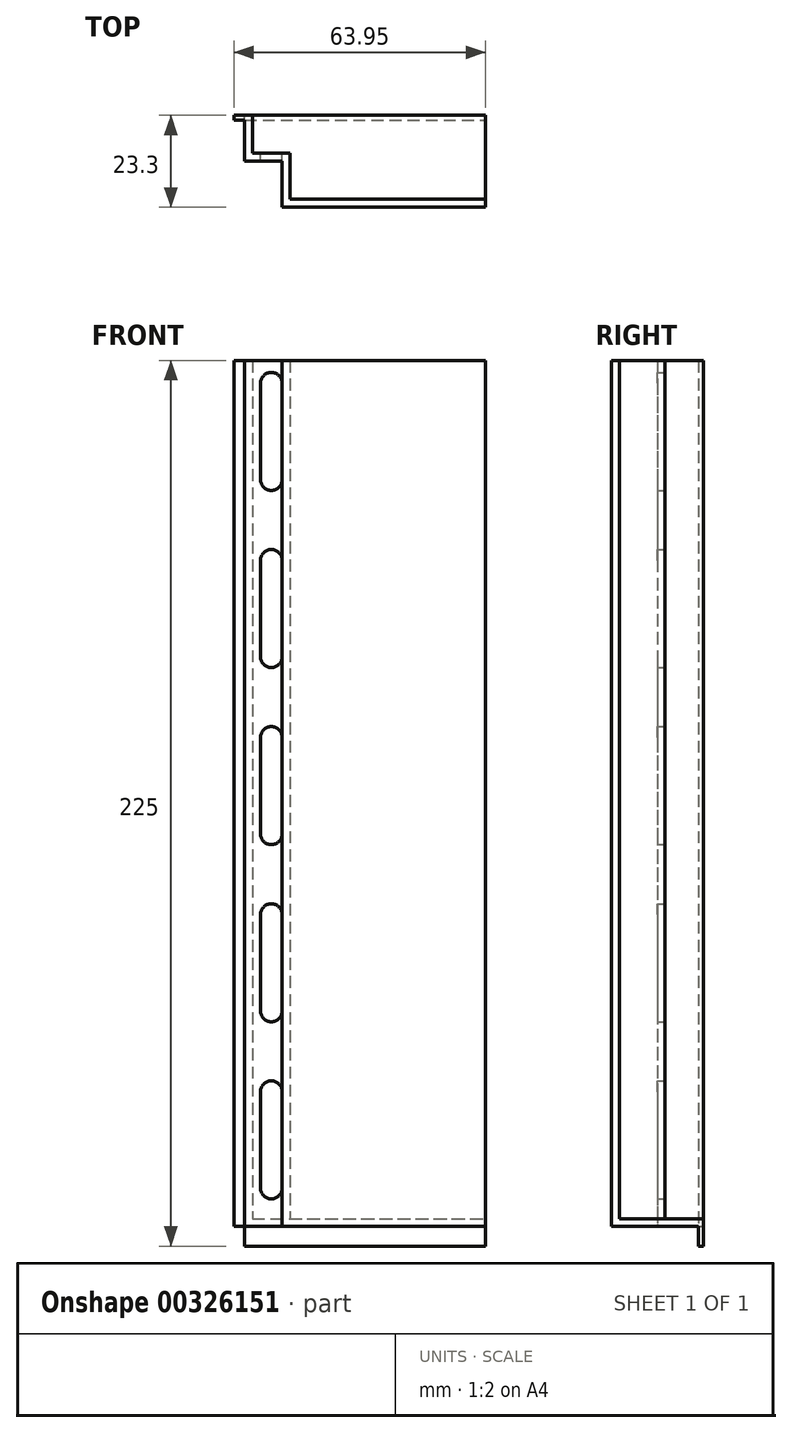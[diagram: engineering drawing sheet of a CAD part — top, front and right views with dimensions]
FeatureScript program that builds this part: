
annotation { "Feature Type Name" : "Feature", "Feature Type Description" : "" }
export const myFeature = defineFeature(function(context is Context, id is Id, definition is map)
    precondition{}
    {
        {
            var Q0;
            Q0=qCreatedBy(makeId("Top.planeOp"),FACE);
            var sketch = newSketch(context, id + "F0", { "sketchPlane" : qUnion([Q0])});
            skLineSegment(sketch, "E0", {"start": v(0, 0) * mm, "end": v(-51.64, 0) * mm});
            skLineSegment(sketch, "E1", {"start": v(-51.64, 0) * mm, "end": v(-51.64, 11.64) * mm});
            skLineSegment(sketch, "E2", {"start": v(-51.64, 11.64) * mm, "end": v(-61.18, 11.64) * mm});
            skLineSegment(sketch, "E3", {"start": v(-61.18, 11.64) * mm, "end": v(-61.18, 22.1) * mm});
            skLineSegment(sketch, "E4", {"start": v(-61.18, 22.1) * mm, "end": v(-63.95, 22.1) * mm});
            skLineSegment(sketch, "E5", {"start": v(-63.95, 22.1) * mm, "end": v(-63.95, 23.3) * mm});
            skLineSegment(sketch, "E6", {"start": v(-63.95, 23.3) * mm, "end": v(-59.18, 23.3) * mm});
            skLineSegment(sketch, "E7", {"start": v(-59.18, 23.3) * mm, "end": v(-59.18, 13.64) * mm});
            skLineSegment(sketch, "E8", {"start": v(-59.18, 13.64) * mm, "end": v(-49.64, 13.64) * mm});
            skLineSegment(sketch, "E9", {"start": v(-49.64, 13.64) * mm, "end": v(-49.64, 2) * mm});
            skLineSegment(sketch, "E10", {"start": v(-49.64, 2) * mm, "end": v(0, 2) * mm});
            skLineSegment(sketch, "E11", {"start": v(0, 2) * mm, "end": v(0, 0) * mm});
            skSolve(sketch);
        }
        {
            var Q0;
            Q0=makeQuery(id+"F0.imprint","IMPRINT",FACE,{"disambiguationData":[TD([[makeQuery(id+"F0.imprint","IMPRINT",EDGE,{"derivedFrom":sQuery(id+"F0.wireOp",EDGE,"E0")}),-1.0]])]});
            extrude(context, id + "F1", {"entities" : qUnion([Q0]), "depth" : 220 * mm, "offsetDistance" : 25 * mm});
        }
        {
            var Q0;
            Q0=makeQuery(id+"F1.opExtrude","SWEPT_FACE",FACE,{"disambiguationData":[OSD([sQuery(id+"F0.wireOp",EDGE,"E8")])]});
            var sketch = newSketch(context, id + "F2", { "sketchPlane" : qUnion([Q0])});
            skLineSegment(sketch, "E12", {"start": v(54.41, 220) * mm, "end": v(54.41, 0) * mm, "construction": true});
            skLineSegment(sketch, "E13", {"start": v(57.18, 214.23) * mm, "end": v(57.18, 189.77) * mm});
            skLineSegment(sketch, "E14", {"start": v(51.64, 214.23) * mm, "end": v(51.64, 189.77) * mm});
            skArc(sketch, "E15", {"start": v(57.18, 214.23) * mm, "mid": v(54.41, 217) * mm, "end": v(51.64, 214.23) * mm});
            skArc(sketch, "E16", {"start": v(51.64, 189.77) * mm, "mid": v(54.41, 187) * mm, "end": v(57.18, 189.77) * mm});
            skArc(sketch, "E17.0.1.0", {"start": v(57.18, 169.23) * mm, "mid": v(54.41, 172) * mm, "end": v(51.64, 169.23) * mm});
            skLineSegment(sketch, "E17.0.1.1", {"start": v(57.18, 169.23) * mm, "end": v(57.18, 144.77) * mm});
            skLineSegment(sketch, "E17.0.1.2", {"start": v(51.64, 169.23) * mm, "end": v(51.64, 144.77) * mm});
            skArc(sketch, "E17.0.1.3", {"start": v(51.64, 144.77) * mm, "mid": v(54.41, 142) * mm, "end": v(57.18, 144.77) * mm});
            skArc(sketch, "E17.0.2.0", {"start": v(57.18, 124.23) * mm, "mid": v(54.41, 127) * mm, "end": v(51.64, 124.23) * mm});
            skLineSegment(sketch, "E17.0.2.1", {"start": v(57.18, 124.23) * mm, "end": v(57.18, 99.77) * mm});
            skLineSegment(sketch, "E17.0.2.2", {"start": v(51.64, 124.23) * mm, "end": v(51.64, 99.77) * mm});
            skArc(sketch, "E17.0.2.3", {"start": v(51.64, 99.77) * mm, "mid": v(54.41, 97) * mm, "end": v(57.18, 99.77) * mm});
            skArc(sketch, "E17.0.3.0", {"start": v(57.18, 79.23) * mm, "mid": v(54.41, 82) * mm, "end": v(51.64, 79.23) * mm});
            skLineSegment(sketch, "E17.0.3.1", {"start": v(57.18, 79.23) * mm, "end": v(57.18, 54.77) * mm});
            skLineSegment(sketch, "E17.0.3.2", {"start": v(51.64, 79.23) * mm, "end": v(51.64, 54.77) * mm});
            skArc(sketch, "E17.0.3.3", {"start": v(51.64, 54.77) * mm, "mid": v(54.41, 52) * mm, "end": v(57.18, 54.77) * mm});
            skArc(sketch, "E17.0.4.0", {"start": v(57.18, 34.23) * mm, "mid": v(54.41, 37) * mm, "end": v(51.64, 34.23) * mm});
            skLineSegment(sketch, "E17.0.4.1", {"start": v(57.18, 34.23) * mm, "end": v(57.18, 9.77) * mm});
            skLineSegment(sketch, "E17.0.4.2", {"start": v(51.64, 34.23) * mm, "end": v(51.64, 9.77) * mm});
            skArc(sketch, "E17.0.4.3", {"start": v(51.64, 9.77) * mm, "mid": v(54.41, 7) * mm, "end": v(57.18, 9.77) * mm});
            skLineSegment(sketch, "E17.direction1", {"start": v(51.64, 189.77) * mm, "end": v(76.64, 189.77) * mm, "construction": true});
            skLineSegment(sketch, "E17.direction2", {"start": v(51.64, 189.77) * mm, "end": v(51.64, 144.77) * mm, "construction": true});
            skSolve(sketch);
        }
        {
            var Q0;
            Q0=makeQuery(id+"F2.imprint","IMPRINT",FACE,{"disambiguationData":[TD([[makeQuery(id+"F2.imprint","IMPRINT",EDGE,{"derivedFrom":sQuery(id+"F2.wireOp",EDGE,"E13")}),-1.0]])]});
            var Q1;
            Q1=makeQuery(id+"F2.imprint","IMPRINT",FACE,{"disambiguationData":[TD([[makeQuery(id+"F2.imprint","IMPRINT",EDGE,{"derivedFrom":sQuery(id+"F2.wireOp",EDGE,"E17.0.1.0")}),1.0]])]});
            var Q2;
            Q2=makeQuery(id+"F2.imprint","IMPRINT",FACE,{"disambiguationData":[TD([[makeQuery(id+"F2.imprint","IMPRINT",EDGE,{"derivedFrom":sQuery(id+"F2.wireOp",EDGE,"E17.0.2.0")}),1.0]])]});
            var Q3;
            Q3=makeQuery(id+"F2.imprint","IMPRINT",FACE,{"disambiguationData":[TD([[makeQuery(id+"F2.imprint","IMPRINT",EDGE,{"derivedFrom":sQuery(id+"F2.wireOp",EDGE,"E17.0.3.0")}),1.0]])]});
            var Q4;
            Q4=makeQuery(id+"F2.imprint","IMPRINT",FACE,{"disambiguationData":[TD([[makeQuery(id+"F2.imprint","IMPRINT",EDGE,{"derivedFrom":sQuery(id+"F2.wireOp",EDGE,"E17.0.4.0")}),1.0]])]});
            var Q5;
            Q5=makeQuery(id+"F1.opExtrude","SWEPT_FACE",FACE,{"disambiguationData":[OSD([sQuery(id+"F0.wireOp",EDGE,"E2")])]});
            extrude(context, id + "F3", {"entities" : qUnion([Q0, Q1, Q2, Q3, Q4]), "operationType" : NewBodyOperationType.REMOVE, "endBound" : BoundingType.UP_TO_SURFACE, "oppositeDirection" : true, "depth" : 25 * mm, "endBoundEntityFace" : qUnion([Q5]), "offsetDistance" : 25 * mm});
        }
        {
            var Q0;
            Q0=makeQuery(id+"F1.opExtrude","CAP_FACE",FACE,{"disambiguationData":[OSD([sQuery(id+"F0.wireOp",EDGE,"E0"),sQuery(id+"F0.wireOp",EDGE,"E1"),sQuery(id+"F0.wireOp",EDGE,"E2"),sQuery(id+"F0.wireOp",EDGE,"E3"),sQuery(id+"F0.wireOp",EDGE,"E4"),sQuery(id+"F0.wireOp",EDGE,"E5"),sQuery(id+"F0.wireOp",EDGE,"E6"),sQuery(id+"F0.wireOp",EDGE,"E7"),sQuery(id+"F0.wireOp",EDGE,"E8"),sQuery(id+"F0.wireOp",EDGE,"E9"),sQuery(id+"F0.wireOp",EDGE,"E10"),sQuery(id+"F0.wireOp",EDGE,"E11")])],"isStart":true});
            var sketch = newSketch(context, id + "F4", { "sketchPlane" : qUnion([Q0])});
            skLineSegment(sketch, "E18", {"start": v(-59.18, -23.3) * mm, "end": v(0, -23.3) * mm});
            skLineSegment(sketch, "E19", {"start": v(0, -23.3) * mm, "end": v(0, -2) * mm});
            skSolve(sketch);
        }
        {
            var Q0;
            Q0=makeQuery(id+"F4.imprint","IMPRINT",FACE,{"disambiguationData":[TD([[makeQuery(id+"F4.imprint","IMPRINT",EDGE,{"derivedFrom":sQuery(id+"F4.wireOp",EDGE,"E18")}),1.0]])]});
            extrude(context, id + "F5", {"entities" : qUnion([Q0]), "operationType" : NewBodyOperationType.ADD, "oppositeDirection" : true, "depth" : 2 * mm, "offsetDistance" : 25 * mm});
        }
        {
            var Q0;
            {var subQ0=sQuery(id+"F0.wireOp",EDGE,"E10");var subQ1=sQuery(id+"F0.wireOp",EDGE,"E9");var subQ2=sQuery(id+"F0.wireOp",EDGE,"E8");var subQ3=sQuery(id+"F0.wireOp",EDGE,"E7");Q0=makeQuery(id+"F5.boolean.opBoolean","MERGE",FACE,{"derivedFrom":[makeQuery(id+"F1.opExtrude","CAP_FACE",FACE,{"disambiguationData":[OSD([sQuery(id+"F0.wireOp",EDGE,"E0"),sQuery(id+"F0.wireOp",EDGE,"E1"),sQuery(id+"F0.wireOp",EDGE,"E2"),sQuery(id+"F0.wireOp",EDGE,"E3"),sQuery(id+"F0.wireOp",EDGE,"E4"),sQuery(id+"F0.wireOp",EDGE,"E5"),sQuery(id+"F0.wireOp",EDGE,"E6"),subQ3,subQ2,subQ1,subQ0,sQuery(id+"F0.wireOp",EDGE,"E11")])],"isStart":true}),makeQuery(id+"F5.opExtrude","CAP_FACE",FACE,{"disambiguationData":[OSD([subQ3,subQ2,subQ1,subQ0,sQuery(id+"F4.wireOp",EDGE,"E18"),sQuery(id+"F4.wireOp",EDGE,"E19")])],"isStart":true})]});}
            var sketch = newSketch(context, id + "F6", { "sketchPlane" : qUnion([Q0])});
            skLineSegment(sketch, "E20", {"start": v(-61.18, -22.1) * mm, "end": v(-61.18, -23.3) * mm});
            skLineSegment(sketch, "E21", {"start": v(-61.18, -22.1) * mm, "end": v(0, -22.1) * mm});
            skSolve(sketch);
        }
        {
            var Q0;
            {var subQ0=sQuery(id+"F6.wireOp",EDGE,"E20");Q0=makeQuery(id+"F6.imprint","IMPRINT",FACE,{"disambiguationData":[TD([[makeQuery(id+"F6.imprint","IMPRINT",EDGE,{"derivedFrom":subQ0}),1.0]])]});}
            extrude(context, id + "F7", {"entities" : qUnion([Q0]), "operationType" : NewBodyOperationType.ADD, "depth" : 5 * mm, "offsetDistance" : 25 * mm});
        }
    });
